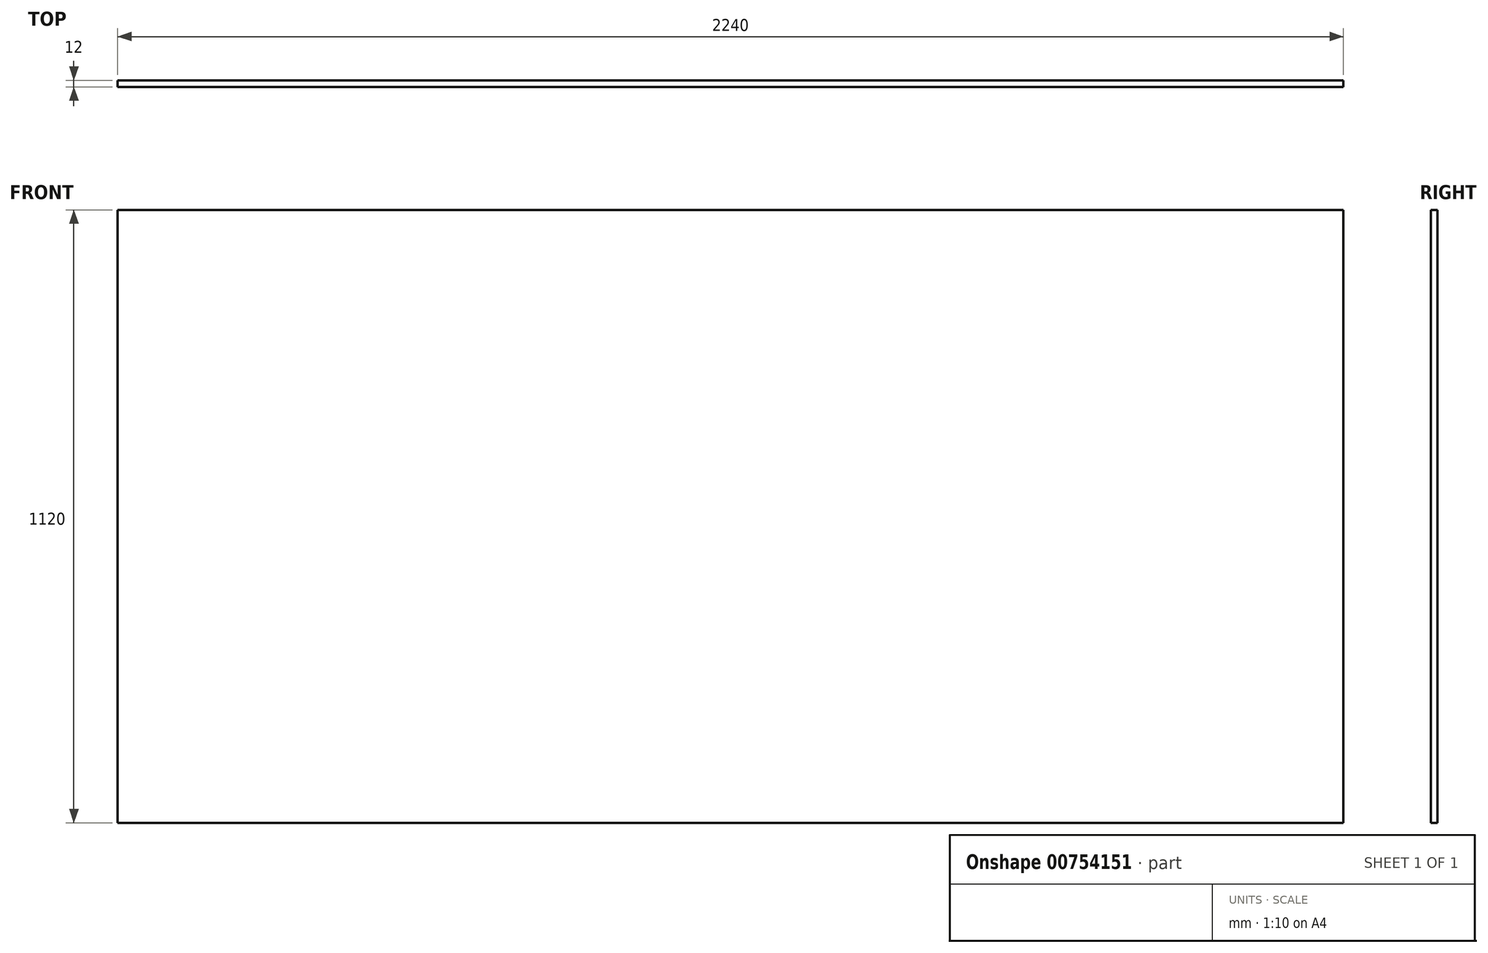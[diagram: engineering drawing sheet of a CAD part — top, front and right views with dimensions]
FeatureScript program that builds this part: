
annotation { "Feature Type Name" : "Feature", "Feature Type Description" : "" }
export const myFeature = defineFeature(function(context is Context, id is Id, definition is map)
    precondition{}
    {
        {
            var Q0;
            Q0=qCreatedBy(makeId("Front.planeOp"),FACE);
            var sketch = newSketch(context, id + "F0", { "sketchPlane" : qUnion([Q0])});
            skLineSegment(sketch, "E0.bottom", {"start": v(0, 0) * mm, "end": v(2240, 0) * mm});
            skLineSegment(sketch, "E0.top", {"start": v(0, 1120) * mm, "end": v(2240, 1120) * mm});
            skLineSegment(sketch, "E0.left", {"start": v(0, 0) * mm, "end": v(0, 1120) * mm});
            skLineSegment(sketch, "E0.right", {"start": v(2240, 0) * mm, "end": v(2240, 1120) * mm});
            skLineSegment(sketch, "E1", {"start": v(0, 100) * mm, "end": v(2240, 100) * mm, "construction": true});
            skSolve(sketch);
        }
        {
            var Q0;
            Q0 = qSketchRegion(id + "F0", true);
            extrude(context, id + "F1", {"entities" : qUnion([Q0]), "depth" : 12 * mm, "offsetDistance" : 25 * mm});
        }
    });
